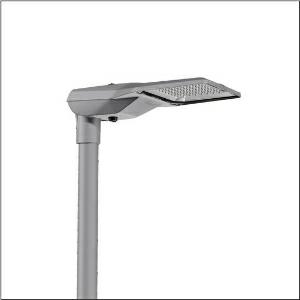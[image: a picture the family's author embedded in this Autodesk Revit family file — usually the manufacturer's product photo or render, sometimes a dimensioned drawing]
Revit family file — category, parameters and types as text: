
# Revit family: streetlight_sl_21_midi___st1_0a_5xe3d23t08lb_1be3
name_source: partatom
category: Lighting Fixtures
units: mm (PartAtom-declared; Revit-internal decimal feet)

## family parameters
Cut with Voids When Loaded = No
Host = Face
Light Source = No
Part Type = Normal
Room Calculation Point = No
Round Connector Dimension = Use Diameter
Shared = No

## types (1)
- --- (1 x LED, 11880 lm, 99.6 W, 2200K)
    Apparent Load = 100 VA
    CIE Flux Codes = 37 72 97 100 100
    Color Rendering = 70
    Color Temperature = 2200K
    Default Elevation = 1800 mm
    Description = Streetlight SL 21 midi, mast luminaire, primary light control with lens, of PMMA, primary optical cover: cover, of toughened safety glass, transparent, light distribution: ST1.0a, light emission: direct distribution, primary light characteristic: asymmetric, installation type: side-entry, post-top, LED, High Power LED, rated luminous flux: 11.880lm, luminous efficacy: 119lm/W, light colour: 722, colour temperature: 2200K, control gear: D4i, control: overheat protection, constant luminous flux control, time-dependent luminous flux control, flexible luminous flux parameterisation, pre-setting: logarithmic dimming characteristic, mains connection: 230..240V, AC, 50/60Hz, start of lifetime: 100W, end of service life: 102W, reduction: 45W, luminaire housing, of diecast aluminium, powder-coated, Siteco® metallic grey (DB 702S), corrosivity category C5 mid according to DIN EN ISO 12944, please order mast flange separately, inclination adjustable: 0°, 5°, 10°, 15°, sealing non-destructively replaceable, multi-level sealing system, length: 644mm, width: 335mm, height: 110mm, mast flange for spigot size: 42mm (side-entry): 5XC10008XM4, 60/48mm (side-entry/post-top): 5XC10108XM2, 76/60mm (side-entry/post-top): 5XC10108XM1, mounting height: 4..8m, Smart Interface below and above, protection rating (complete): IP66, insulation class (complete): insulation class II (safety insulation), certification: CE, ENEC, ENEC+, VDE, impact resistance: IK10, permissible operating ambient temperature for outdoor applications: -40..+50°C, standard-compliant lighting for roads and squares, packaging unit: 1 piece

Light Distribution: ST1.0a
    Height = 111 mm
    Lamp = 1 x LED
    Lamp Light Flux = 11880 lm
    Lamp Power = 99.6 W
    Lamp count = 1
    Length = 644 mm
    Luminous efficacy = 119 lm/W
    Manufacturer = Siteco
    ModVariant = No
    Model = 5XE3D23T08LB
    Number of Poles = 1
    OnlyDefault = Yes
    Power Factor = 1
    Product Name = Streetlight SL 21 midi | ST1.0a
    Product group = mast luminaire | pylon top
    ProductGroupID = 6100
    Protection Class = Protection class II
    Protection Degree = IP 66
    RLX_Detail_Level = 1
    RLX_Emergency_Light_Flux = 0 lm
    RLX_Emergency_Type = 0
    RLX_Emergency_Type_DB = No
    RlxData = <blob elided: 26893 chars, md5=0242169c>
    Socket = socket
    Standby Power = 0 W
    System Light Flux = 11880 lm
    System Power = 100 W
    Type Comments = factory setting: luminous flux: 100 % | dim-lin: 254 | 1020 mA
    Type Image = l_1004304.jpg
    URL = http://relux.com
    VarID = @adj_012251
    Voltage = 0 V
    Weight = 0.00 kg
    Width = 336 mm

## geometry (parser evidence)
native form markers: Blend x4, Sweep x12
no freeform markers — native parametric forms only
